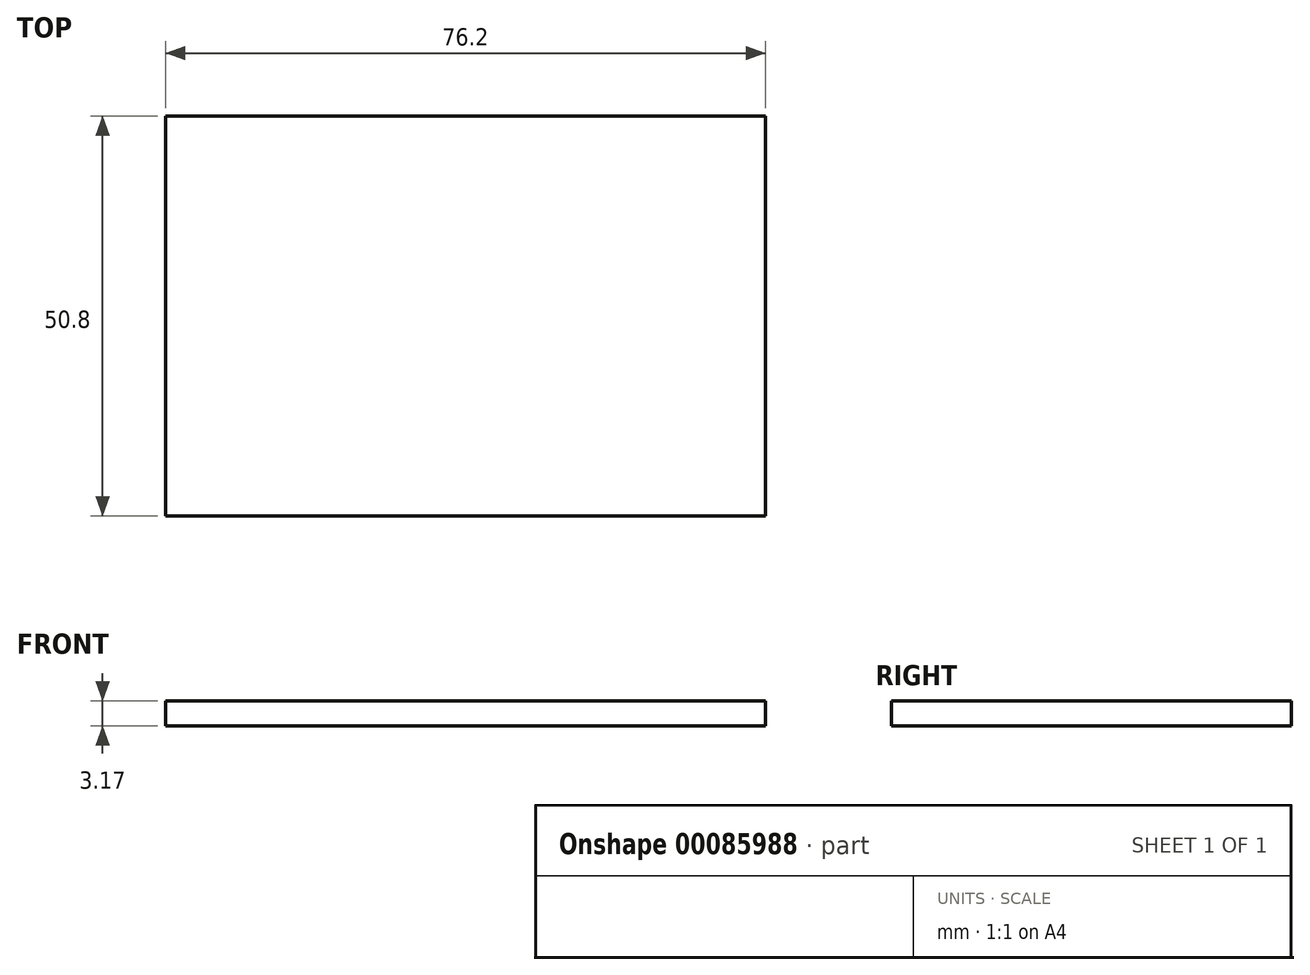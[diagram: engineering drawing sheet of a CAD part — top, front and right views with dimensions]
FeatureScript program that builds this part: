
annotation { "Feature Type Name" : "Feature", "Feature Type Description" : "" }
export const myFeature = defineFeature(function(context is Context, id is Id, definition is map)
    precondition{}
    {
        {
            var Q0;
            Q0=qCreatedBy(makeId("Top.planeOp"),FACE);
            var sketch = newSketch(context, id + "F0", { "sketchPlane" : qUnion([Q0])});
            skLineSegment(sketch, "E0.bottom", {"start": v(-31.18, 0) * mm, "end": v(45.02, 0) * mm});
            skLineSegment(sketch, "E0.top", {"start": v(-31.18, 50.8) * mm, "end": v(45.02, 50.8) * mm});
            skLineSegment(sketch, "E0.left", {"start": v(-31.18, 0) * mm, "end": v(-31.18, 50.8) * mm});
            skLineSegment(sketch, "E0.right", {"start": v(45.02, 0) * mm, "end": v(45.02, 50.8) * mm});
            skSolve(sketch);
        }
        {
            var Q0;
            Q0 = qSketchRegion(id + "F0", true);
            extrude(context, id + "F1", {"entities" : qUnion([Q0]), "depth" : 3.17 * mm});
        }
    });
